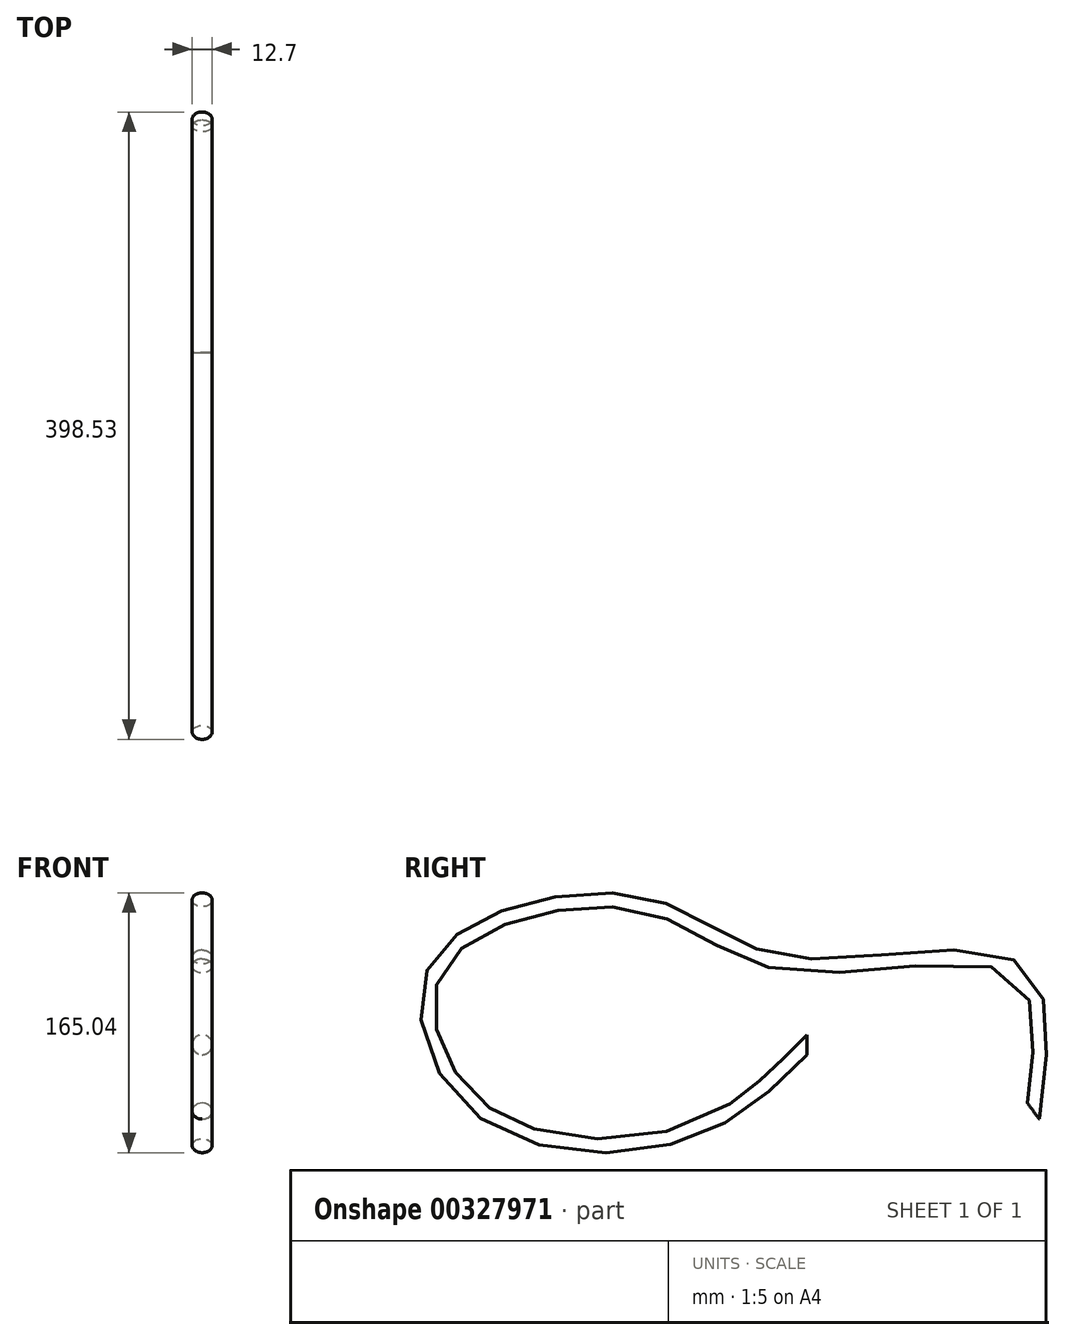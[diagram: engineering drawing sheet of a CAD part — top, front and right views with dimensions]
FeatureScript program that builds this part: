
annotation { "Feature Type Name" : "Feature", "Feature Type Description" : "" }
export const myFeature = defineFeature(function(context is Context, id is Id, definition is map)
    precondition{}
    {
        {
            var Q0;
            Q0=qCreatedBy(makeId("Right.planeOp"),FACE);
            var sketch = newSketch(context, id + "F0", { "sketchPlane" : qUnion([Q0])});
            skFitSpline(sketch, "E0", {"points": [v(0, 0) * mm, v(-76.78, -55.92) * mm, v(-204.06, -43.4) * mm, v(-239.95, 36.3) * mm, v(-191.54, 80.96) * mm, v(-94.73, 86.8) * mm, v(-11.27, 51.33) * mm, v(131.87, 48.4) * mm, v(143.97, -42.15) * mm], "startDerivative": vector(-529.43, -545.23) * mm, "endDerivative": vector(-125.6, -954.33) * mm});
            skSolve(sketch);
        }
        {
            var Q0;
            Q0=qCreatedBy(makeId("Front.planeOp"),FACE);
            var sketch = newSketch(context, id + "F1", { "sketchPlane" : qUnion([Q0])});
            skCircle(sketch, "E1", {"center": v(0, 0) * mm, "radius": 6.35 * mm});
            skSolve(sketch);
        }
        {
            var Q0;
            Q0=makeQuery(id+"F1.imprint","IMPRINT",FACE,{"disambiguationData":[TD([[makeQuery(id+"F1.imprint","IMPRINT",EDGE,{"derivedFrom":sQuery(id+"F1.wireOp",EDGE,"E1")}),1.0]])]});
            var Q1;
            Q1=sQuery(id+"F0.wireOp",EDGE,"E0");
            sweep(context, id + "F2", {"profiles" : qUnion([Q0]), "path" : qUnion([Q1])});
        }
    });
